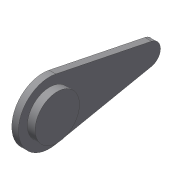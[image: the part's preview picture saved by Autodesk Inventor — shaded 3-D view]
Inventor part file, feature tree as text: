
AUTODESK INVENTOR PART (.ipt)
format: ipt  version: 2019.4 (Build 234330000, 330)  size: 112,640 bytes
history: native  units: mm
features: extrude x3, sketch x3, other x1
ambient origin geometry x8: Origin, YZ Plane, XZ Plane, XY Plane, X Axis, Y Axis, Z Axis, Center Point
bodies: Body1 (feature_tree)
feature tree (7):
  other  "ソリッド1"
  extrude  "押し出し1"  Depth=20.0mm
  extrude  "押し出し2"  Depth=28.0mm
  extrude  "押し出し3"  Depth=10.0mm
  sketch  "スケッチ1"
  sketch  "スケッチ2"
  sketch  "スケッチ3"
